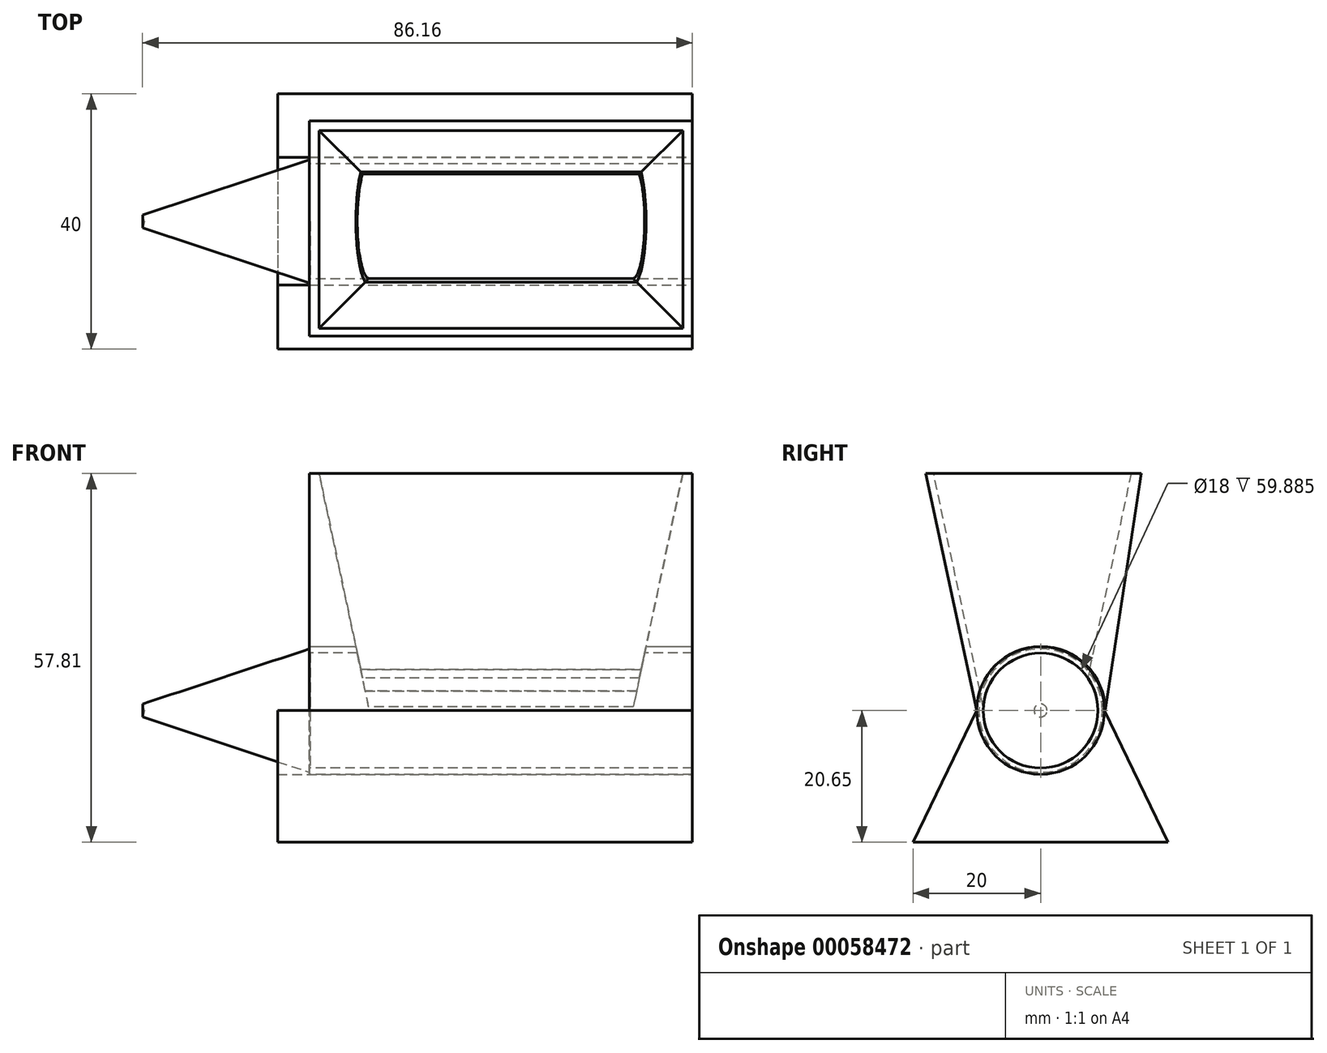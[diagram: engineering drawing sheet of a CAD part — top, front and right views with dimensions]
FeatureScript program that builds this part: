
annotation { "Feature Type Name" : "Feature", "Feature Type Description" : "" }
export const myFeature = defineFeature(function(context is Context, id is Id, definition is map)
    precondition{}
    {
        {
            var Q0;
            Q0=qCreatedBy(makeId("Front.planeOp"),FACE);
            var sketch = newSketch(context, id + "F0", { "sketchPlane" : qUnion([Q0])});
            skLineSegment(sketch, "E0.bottom", {"start": v(-27.47, 0) * mm, "end": v(32.53, 0) * mm});
            skLineSegment(sketch, "E0.top", {"start": v(-27.47, 10) * mm, "end": v(32.53, 10) * mm});
            skLineSegment(sketch, "E0.left", {"start": v(-27.47, 0) * mm, "end": v(-27.47, 10) * mm});
            skLineSegment(sketch, "E0.right", {"start": v(32.53, 0) * mm, "end": v(32.53, 10) * mm});
            skSolve(sketch);
        }
        {
            var Q0;
            Q0 = qSketchRegion(id + "F0", true);
            var Q1;
            Q1=sQuery(id+"F0.wireOp",EDGE,"E0.bottom");
            revolve(context, id + "F1", {"entities" : qUnion([Q0]), "axis" : qUnion([Q1]), "revolveType" : RevolveType.FULL});
        }
        {
            var Q0;
            Q0=makeQuery(id+"F1.opRevolve","SWEPT_FACE",FACE,{"disambiguationData":[OSD([sQuery(id+"F0.wireOp",EDGE,"E0.left")])]});
            var sketch = newSketch(context, id + "F2", { "sketchPlane" : qUnion([Q0])});
            skCircle(sketch, "E1", {"center": v(0, 0) * mm, "radius": 9 * mm});
            skSolve(sketch);
        }
        {
            var Q0;
            Q0=makeQuery(id+"F2.imprint","IMPRINT",FACE,{"disambiguationData":[TD([[makeQuery(id+"F2.imprint","IMPRINT",EDGE,{"derivedFrom":sQuery(id+"F2.wireOp",EDGE,"E1")}),1.0]])]});
            extrude(context, id + "F3", {"entities" : qUnion([Q0]), "operationType" : NewBodyOperationType.REMOVE, "oppositeDirection" : true, "depth" : 60 * mm});
        }
        {
            var Q0;
            Q0=qCreatedBy(makeId("Front.planeOp"),FACE);
            var sketch = newSketch(context, id + "F4", { "sketchPlane" : qUnion([Q0])});
            skLineSegment(sketch, "E2", {"start": v(-27.35, 9.72) * mm, "end": v(-27.35, 0) * mm});
            skLineSegment(sketch, "E3", {"start": v(-27.35, 0) * mm, "end": v(-53.35, 0) * mm});
            skLineSegment(sketch, "E4", {"start": v(-53.63, 1.02) * mm, "end": v(-27.35, 9.72) * mm});
            skLineSegment(sketch, "E5", {"start": v(-53.63, 1.02) * mm, "end": v(-53.35, 0) * mm});
            skSolve(sketch);
        }
        {
            var Q0;
            Q0 = qSketchRegion(id + "F4", true);
            var Q1;
            Q1=sQuery(id+"F0.wireOp",EDGE,"E0.bottom");
            revolve(context, id + "F5", {"operationType" : NewBodyOperationType.ADD, "entities" : qUnion([Q0]), "axis" : qUnion([Q1]), "revolveType" : RevolveType.FULL});
        }
        {
            var Q0;
            Q0=makeQuery(id+"F1.opRevolve","SWEPT_FACE",FACE,{"disambiguationData":[OSD([sQuery(id+"F0.wireOp",EDGE,"E0.right")])]});
            var sketch = newSketch(context, id + "F6", { "sketchPlane" : qUnion([Q0])});
            skLineSegment(sketch, "E6", {"start": v(-10, 0) * mm, "end": v(-18, 37.16) * mm});
            skLineSegment(sketch, "E7", {"start": v(-18, 37.16) * mm, "end": v(15.76, 37.16) * mm});
            skLineSegment(sketch, "E8", {"start": v(15.76, 37.16) * mm, "end": v(10.11, 0) * mm});
            skArc(sketch, "E9", {"start": v(10.11, 0) * mm, "mid": v(0.06, 10.06) * mm, "end": v(-10, 0) * mm});
            skSolve(sketch);
        }
        {
            var Q0;
            Q0 = qSketchRegion(id + "F6", true);
            extrude(context, id + "F7", {"entities" : qUnion([Q0]), "oppositeDirection" : true, "depth" : 60 * mm});
        }
        {
            var Q0;
            Q0=makeQuery(id+"F7.opExtrude","SWEPT_FACE",FACE,{"disambiguationData":[OSD([sQuery(id+"F6.wireOp",EDGE,"E7")])]});
            var sketch = newSketch(context, id + "F8", { "sketchPlane" : qUnion([Q0])});
            skLineSegment(sketch, "E10.bottom", {"start": v(-25.97, 14.25) * mm, "end": v(31.03, 14.25) * mm});
            skLineSegment(sketch, "E10.top", {"start": v(-25.97, -16.75) * mm, "end": v(31.03, -16.75) * mm});
            skLineSegment(sketch, "E10.left", {"start": v(-25.97, 14.25) * mm, "end": v(-25.97, -16.75) * mm});
            skLineSegment(sketch, "E10.right", {"start": v(31.03, 14.25) * mm, "end": v(31.03, -16.75) * mm});
            skSolve(sketch);
        }
        {
            var Q0;
            Q0 = qSketchRegion(id + "F8", true);
            extrude(context, id + "F9", {"entities" : qUnion([Q0]), "operationType" : NewBodyOperationType.REMOVE, "oppositeDirection" : true, "depth" : 37 * mm, "hasDraft" : true, "draftAngle" : 12 * degree, "draftPullDirection" : true});
        }
        {
            var Q0;
            Q0=makeQuery(id+"F1.opRevolve","SWEPT_FACE",FACE,{"disambiguationData":[OSD([sQuery(id+"F0.wireOp",EDGE,"E0.right")])]});
            var sketch = newSketch(context, id + "F10", { "sketchPlane" : qUnion([Q0])});
            skLineSegment(sketch, "E11", {"start": v(-10, 0) * mm, "end": v(-20, -20.65) * mm});
            skLineSegment(sketch, "E12", {"start": v(10, 0) * mm, "end": v(20, -20.65) * mm});
            skLineSegment(sketch, "E13", {"start": v(20, -20.65) * mm, "end": v(-20, -20.65) * mm});
            skArc(sketch, "E14", {"start": v(-10, 0) * mm, "mid": v(0, -10) * mm, "end": v(10, 0) * mm});
            skSolve(sketch);
        }
        {
            var Q0;
            Q0=makeQuery(id+"F10.imprint","IMPRINT",FACE,{"disambiguationData":[TD([[makeQuery(id+"F10.imprint","IMPRINT",EDGE,{"derivedFrom":sQuery(id+"F10.wireOp",EDGE,"E11")}),1.0]])]});
            extrude(context, id + "F11", {"entities" : qUnion([Q0]), "oppositeDirection" : true, "depth" : 65 * mm});
        }
    });
